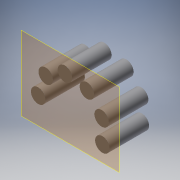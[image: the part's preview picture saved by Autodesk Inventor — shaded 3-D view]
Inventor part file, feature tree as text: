
AUTODESK INVENTOR PART (.ipt)
format: ipt  version: 2019 (Build 230136000, 136)  size: 112,128 bytes
history: native  units: mm
features: other x3, plane x1, extrude x1, sketch x1, reference x1
ambient origin geometry x8: Origin, YZ Plane, XZ Plane, XY Plane, X Axis, Y Axis, Z Axis, Center Point
bodies: Solid1 (feature_tree)
feature tree (7):
  plane  "Work Plane1"
  extrude  "Extrusion1"  [1 undecoded]
  sketch  "Sketch1"  dims[d0=30.0mm d1=0.0mm]
  reference  "Reference1"
  parser-record x1  (decoder bookkeeping rows leaked as tree rows — omitted from the tree; the rows remain in map.json)
  other  "mount assem.iam"
  other  "mounter:1"
note: 1 required parameter value undecoded (feature->parameter linkage not recoverable at this tier; creation-order binding heuristic only, values carry confidence <= 0.55)
note: 1 file-system path scrubbed to <path> (originals preserved in map.json)
